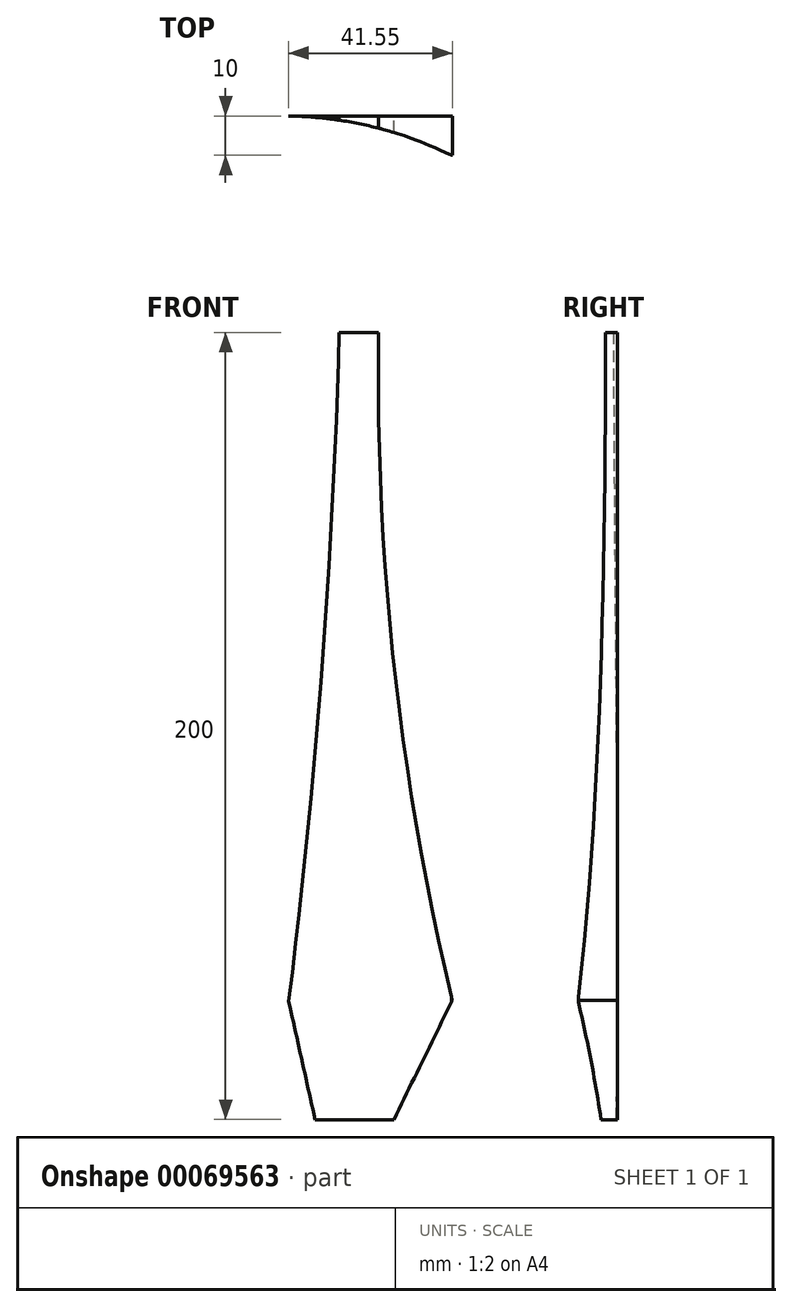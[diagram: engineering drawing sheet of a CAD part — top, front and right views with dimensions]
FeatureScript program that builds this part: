
annotation { "Feature Type Name" : "Feature", "Feature Type Description" : "" }
export const myFeature = defineFeature(function(context is Context, id is Id, definition is map)
    precondition{}
    {
        {
            var Q0;
            Q0=qCreatedBy(makeId("Front.planeOp"),FACE);
            var sketch = newSketch(context, id + "F0", { "sketchPlane" : qUnion([Q0])});
            skLineSegment(sketch, "E0.bottom", {"start": v(-25.02, 104.39) * mm, "end": v(16.56, 104.39) * mm});
            skLineSegment(sketch, "E0.top", {"start": v(-25.02, -95.61) * mm, "end": v(16.56, -95.61) * mm});
            skLineSegment(sketch, "E0.left", {"start": v(-25.02, 104.39) * mm, "end": v(-25.02, -95.61) * mm});
            skLineSegment(sketch, "E0.right", {"start": v(16.56, 104.39) * mm, "end": v(16.56, -95.61) * mm});
            skSolve(sketch);
        }
        {
            var Q0;
            Q0 = qSketchRegion(id + "F0", true);
            extrude(context, id + "F1", {"entities" : qUnion([Q0]), "depth" : 10 * mm});
        }
        {
            var Q0;
            Q0=qCreatedBy(makeId("Top.planeOp"),FACE);
            var sketch = newSketch(context, id + "F2", { "sketchPlane" : qUnion([Q0])});
            skArc(sketch, "E1", {"start": v(16.7, -10.17) * mm, "mid": v(-3.58, -2.77) * mm, "end": v(-24.99, 0) * mm});
            skSolve(sketch);
        }
        {
            var Q0;
            Q0=makeQuery(id+"F1.opExtrude","SWEPT_FACE",FACE,{"disambiguationData":[OSD([sQuery(id+"F0.wireOp",EDGE,"E0.bottom")])]});
            var sketch = newSketch(context, id + "F3", { "sketchPlane" : qUnion([Q0])});
            skArc(sketch, "E2.0", {"start": v(16.7, -10.17) * mm, "mid": v(-3.58, -2.77) * mm, "end": v(-24.99, 0) * mm});
            skSolve(sketch);
        }
        {
            var Q0;
            {var subQ1=sQuery(id+"F0.wireOp",EDGE,"E0.bottom");var subQ6=makeQuery(id+"F1.opExtrude","SWEPT_EDGE",EDGE,{"disambiguationData":[OSD([subQ1,sQuery(id+"F0.wireOp",EDGE,"E0.left")])]});Q0=makeQuery(id+"F3.imprint","IMPRINT",FACE,{"disambiguationData":[TD([[makeQuery(id+"F3.imprint","IMPRINT",EDGE,{"derivedFrom":subQ6}),-1.0]])]});}
            extrude(context, id + "F4", {"entities" : qUnion([Q0]), "operationType" : NewBodyOperationType.REMOVE, "endBound" : BoundingType.THROUGH_ALL, "oppositeDirection" : true, "depth" : 25.4 * mm});
        }
        {
            var Q0;
            Q0=makeQuery(id+"F1.opExtrude","CAP_FACE",FACE,{"disambiguationData":[OSD([sQuery(id+"F0.wireOp",EDGE,"E0.bottom"),sQuery(id+"F0.wireOp",EDGE,"E0.top"),sQuery(id+"F0.wireOp",EDGE,"E0.left"),sQuery(id+"F0.wireOp",EDGE,"E0.right")])],"isStart":true});
            var sketch = newSketch(context, id + "F5", { "sketchPlane" : qUnion([Q0])});
            skLineSegment(sketch, "E3", {"start": v(2.16, 104.39) * mm, "end": v(12.16, 104.39) * mm});
            skLineSegment(sketch, "E4", {"start": v(24.99, -95.61) * mm, "end": v(24.99, -65.61) * mm});
            skArc(sketch, "E5", {"start": v(12.16, 104.39) * mm, "mid": v(16.55, 19.23) * mm, "end": v(24.99, -65.61) * mm});
            skArc(sketch, "E6", {"start": v(-16.56, -65.34) * mm, "mid": v(-1.85, 18.93) * mm, "end": v(2.16, 104.39) * mm});
            skLineSegment(sketch, "E7", {"start": v(-1.7, -95.61) * mm, "end": v(18.3, -95.61) * mm});
            skLineSegment(sketch, "E8", {"start": v(-16.56, -65.34) * mm, "end": v(-1.7, -95.61) * mm});
            skLineSegment(sketch, "E9", {"start": v(24.99, -65.61) * mm, "end": v(18.3, -95.61) * mm});
            skSolve(sketch);
        }
        {
            var Q0;
            {var subQ0=sQuery(id+"F5.wireOp",EDGE,"E5");Q0=makeQuery(id+"F5.imprint","IMPRINT",FACE,{"disambiguationData":[TD([[makeQuery(id+"F5.imprint","IMPRINT",EDGE,{"derivedFrom":subQ0}),1.0]])]});}
            var Q1;
            {var subQ0=sQuery(id+"F5.wireOp",EDGE,"E6");Q1=makeQuery(id+"F5.imprint","IMPRINT",FACE,{"disambiguationData":[TD([[makeQuery(id+"F5.imprint","IMPRINT",EDGE,{"derivedFrom":subQ0}),1.0]])]});}
            var Q2;
            {var subQ0=sQuery(id+"F5.wireOp",EDGE,"E8");Q2=makeQuery(id+"F5.imprint","IMPRINT",FACE,{"disambiguationData":[TD([[makeQuery(id+"F5.imprint","IMPRINT",EDGE,{"derivedFrom":subQ0}),-1.0]])]});}
            var Q3;
            {var subQ0=sQuery(id+"F5.wireOp",EDGE,"E4");Q3=makeQuery(id+"F5.imprint","IMPRINT",FACE,{"disambiguationData":[TD([[makeQuery(id+"F5.imprint","IMPRINT",EDGE,{"derivedFrom":subQ0}),1.0]])]});}
            extrude(context, id + "F6", {"entities" : qUnion([Q0, Q1, Q2, Q3]), "operationType" : NewBodyOperationType.REMOVE, "endBound" : BoundingType.THROUGH_ALL, "oppositeDirection" : true, "depth" : 25.4 * mm});
        }
    });
